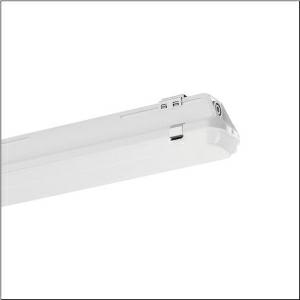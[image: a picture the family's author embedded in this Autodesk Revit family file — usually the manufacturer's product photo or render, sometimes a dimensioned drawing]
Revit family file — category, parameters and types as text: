
# Revit family: monsun_r__21_51fb10dp440b_4f1d
name_source: partatom
category: Lighting Fixtures
units: mm (PartAtom-declared; Revit-internal decimal feet)

## family parameters
Cut with Voids When Loaded = No
Host = Face
Light Source = No
Part Type = Normal
Room Calculation Point = No
Round Connector Dimension = Use Diameter
Shared = No

## types (1)
- --- (1 x LED, 4360 lm, 27.9 W, 4000K)
    Apparent Load = 28 VA
    CIE Flux Codes = 47 77 93 94 100
    Color Rendering = 80
    Color Temperature = 4000K
    Default Elevation = 1800 mm
    Description = Monsun® 21, damp-proof luminaire, chain hanger, primary optical cover: enclosure, of PMMA, light emission: direct distribution, primary light characteristic: symmetric, installation type: suspended mounting, surface-mounted, horizontal mounting, vertical mounting, LED, rated luminous flux: 4.360lm, luminous efficacy: 156lm/W, light colour: 840, colour temperature: 4000K, control gear: ECG DALI, with terminal, 5-pole, max. 2.5mm², mains connection: 220..240V, AC, 50/60Hz, rated input power: 28W, housing, of glass-fibre reinforced polyester, uncoated, bright grey, length: 1.590mm, width: 90mm, height: 88mm, clip for enclosure, of stainless steel (V2A), ceiling mounting element, of stainless steel (V2A), chain hanger, of stainless steel (V2A), protection rating (complete): IP66, insulation class (complete): insulation class I (protective earthing), certification: CE, ENEC, VDE, UKCA, protection symbol: D, impact resistance: IK04, permissible operating ambient temperature: -25..+35°C, standard: EN 50419, EN 60598-2-1, corresponds to IFS (International Featured Standards) requirements for safety and quality in the food industry, for indoor or canopied outdoor use, no direct snow, no direct sun, no direct rain, packaging unit: 1 piece
    Height = 89 mm
    Lamp = 1 x LED
    Lamp Light Flux = 4360 lm
    Lamp Power = 27.9 W
    Lamp count = 1
    Length = 1590 mm
    Luminous efficacy = 156 lm/W
    Manufacturer = Siteco
    ModVariant = No
    Model = 51FB10DP440B
    Mounting Place = Ceiling
    Mounting Type = Pendant
    Number of Poles = 1
    OnlyDefault = Yes
    Power Factor = 1
    Product Name = Monsun® 21
    Product group = damp-proof luminaire | ceiling pendant
    ProductGroupID = 908
    Protection Class = Protection class I
    Protection Degree = IP 66
    RLX_Detail_Level = 1
    RlxData = <blob elided: 91589 chars, md5=6d1b19cd>
    Socket = socket
    Standby Power = 0 W
    System Light Flux = 4360 lm
    System Power = 28 W
    Type Comments = factory setting: luminous flux: 100 % | dim-lin: 254 | 184 mA
    Type Image = l_1006717.jpg
    URL = http://relux.com
    VarID = @adj_125339
    Voltage = 0 V
    Weight = 0.00 kg
    Width = 90 mm

## geometry (parser evidence)
native form markers: Blend x4, Sweep x13
no freeform markers — native parametric forms only
